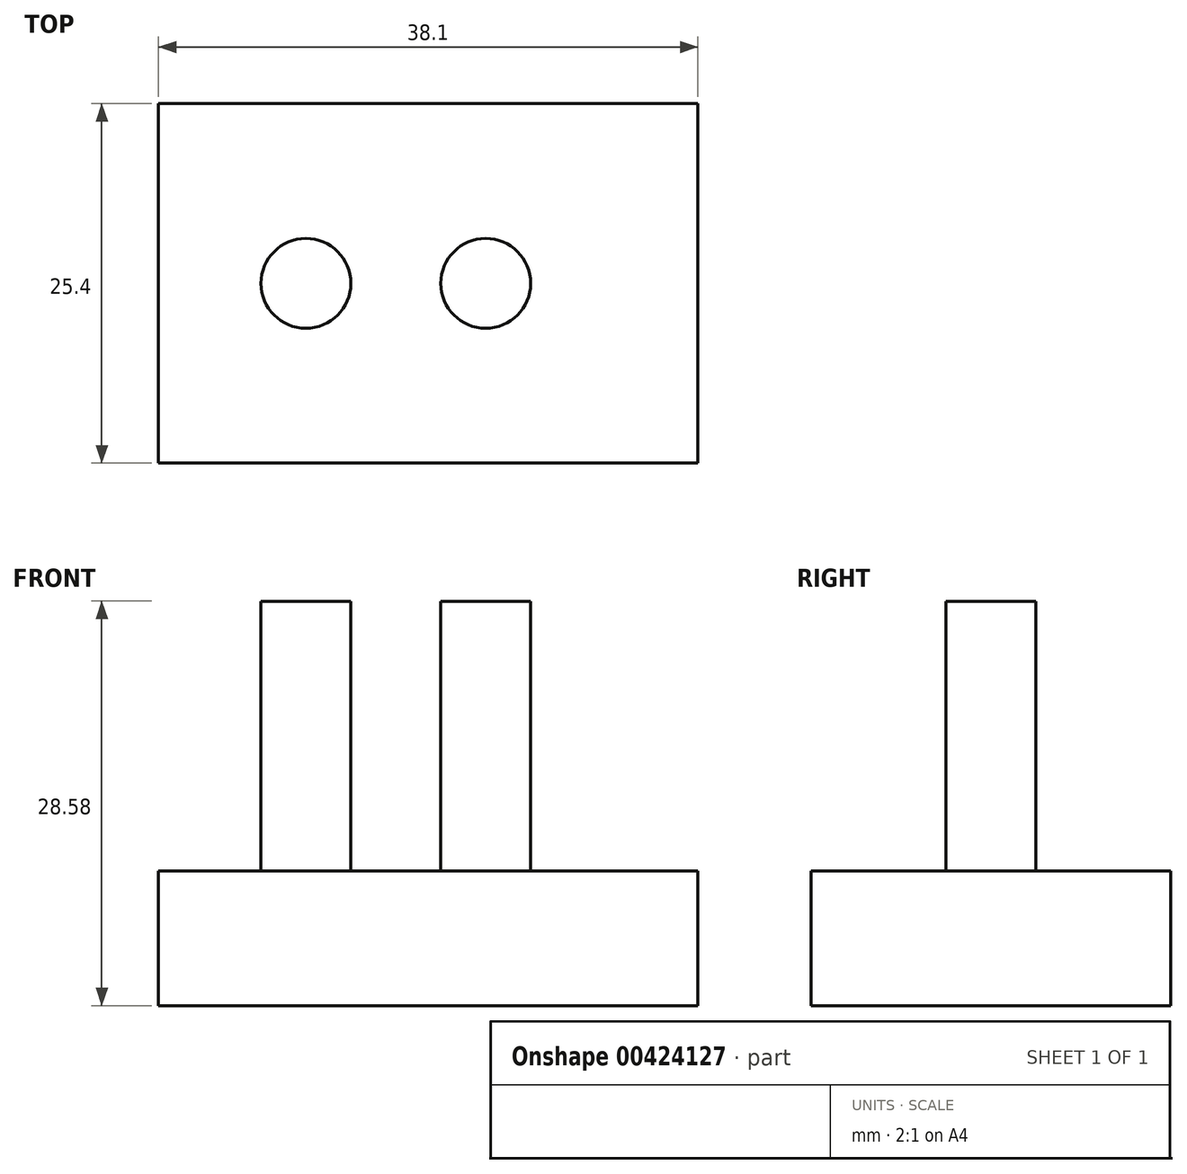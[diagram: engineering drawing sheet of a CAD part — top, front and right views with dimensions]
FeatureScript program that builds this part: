
annotation { "Feature Type Name" : "Feature", "Feature Type Description" : "" }
export const myFeature = defineFeature(function(context is Context, id is Id, definition is map)
    precondition{}
    {
        {
            var Q0;
            Q0=qCreatedBy(makeId("Top.planeOp"),FACE);
            var sketch = newSketch(context, id + "F0", { "sketchPlane" : qUnion([Q0])});
            skLineSegment(sketch, "E0.bottom", {"start": v(0, 0) * mm, "end": v(38.1, 0) * mm});
            skLineSegment(sketch, "E0.top", {"start": v(0, 25.4) * mm, "end": v(38.1, 25.4) * mm});
            skLineSegment(sketch, "E0.left", {"start": v(0, 0) * mm, "end": v(0, 25.4) * mm});
            skLineSegment(sketch, "E0.right", {"start": v(38.1, 0) * mm, "end": v(38.1, 25.4) * mm});
            skSolve(sketch);
        }
        {
            var Q0;
            Q0 = qSketchRegion(id + "F0", true);
            extrude(context, id + "F1", {"entities" : qUnion([Q0]), "depth" : 9.52 * mm});
        }
        {
            var Q0;
            Q0=makeQuery(id+"F1.opExtrude","CAP_FACE",FACE,{"disambiguationData":[OSD([sQuery(id+"F0.wireOp",EDGE,"E0.bottom"),sQuery(id+"F0.wireOp",EDGE,"E0.top"),sQuery(id+"F0.wireOp",EDGE,"E0.left"),sQuery(id+"F0.wireOp",EDGE,"E0.right")])],"isStart":false});
            var sketch = newSketch(context, id + "F2", { "sketchPlane" : qUnion([Q0])});
            skCircle(sketch, "E1", {"center": v(10.41, 12.7) * mm, "radius": 3.18 * mm});
            skPoint(sketch, "E1.centerSnap0", {"position": v(0, 12.7) * mm});
            skCircle(sketch, "E2", {"center": v(23.11, 12.7) * mm, "radius": 3.18 * mm});
            skSolve(sketch);
        }
        {
            var Q0;
            Q0 = qSketchRegion(id + "F2", true);
            extrude(context, id + "F3", {"entities" : qUnion([Q0]), "operationType" : NewBodyOperationType.ADD, "depth" : 19.05 * mm});
        }
    });
